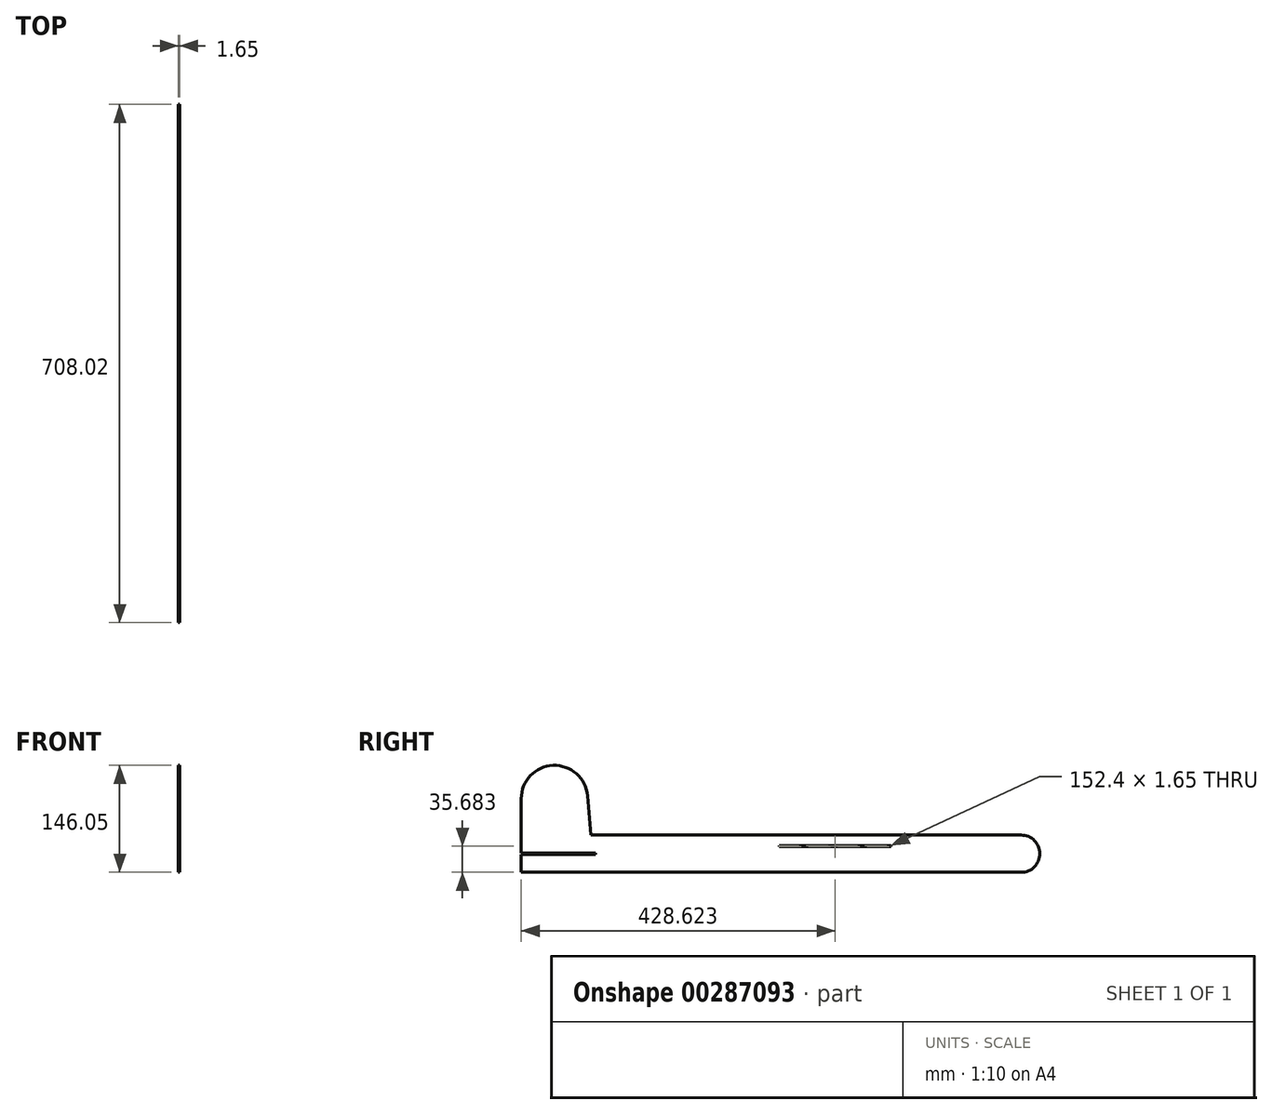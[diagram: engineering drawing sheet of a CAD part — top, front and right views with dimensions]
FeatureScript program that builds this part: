
annotation { "Feature Type Name" : "Feature", "Feature Type Description" : "" }
export const myFeature = defineFeature(function(context is Context, id is Id, definition is map)
    precondition{}
    {
        {
            var Q0;
            Q0=qCreatedBy(makeId("Right.planeOp"),FACE);
            var sketch = newSketch(context, id + "F0", { "sketchPlane" : qUnion([Q0])});
            skLineSegment(sketch, "E0.bottom", {"start": v(-246.06, 25.4) * mm, "end": v(341.31, 25.4) * mm});
            skLineSegment(sketch, "E0.top", {"start": v(-341.31, -25.4) * mm, "end": v(341.31, -25.4) * mm});
            skLineSegment(sketch, "E0.left", {"start": v(-341.31, 25.4) * mm, "end": v(-341.31, -25.4) * mm});
            skPoint(sketch, "E0.middle", {"position": v(0, 0) * mm});
            skLineSegment(sketch, "E1", {"start": v(-246.06, 25.4) * mm, "end": v(-250.77, 79.25) * mm});
            skLineSegment(sketch, "E2", {"start": v(-341.31, 75.3) * mm, "end": v(-341.31, 25.4) * mm});
            skArc(sketch, "E3", {"start": v(-250.77, 79.25) * mm, "mid": v(-297.94, 120.6) * mm, "end": v(-341.31, 75.3) * mm});
            skArc(sketch, "E4", {"start": v(341.31, -25.4) * mm, "mid": v(366.71, 0) * mm, "end": v(341.31, 25.4) * mm});
            skPoint(sketch, "E4.third.point", {"position": v(365.34, 8.24) * mm});
            skSolve(sketch);
        }
        {
            var Q0;
            Q0=makeQuery(id+"F0.imprint","IMPRINT",FACE,{"disambiguationData":[TD([[makeQuery(id+"F0.imprint","IMPRINT",EDGE,{"derivedFrom":sQuery(id+"F0.wireOp",EDGE,"E0.bottom")}),-1.0]])]});
            extrude(context, id + "F1", {"entities" : qUnion([Q0]), "depth" : 1.65 * mm});
        }
        {
            var Q0;
            Q0=makeQuery(id+"F0.imprint","IMPRINT",FACE,{"disambiguationData":[TD([[makeQuery(id+"F0.imprint","IMPRINT",EDGE,{"derivedFrom":sQuery(id+"F0.wireOp",EDGE,"E0.bottom")}),-1.0]])]});
            var sketch = newSketch(context, id + "F2", { "sketchPlane" : qUnion([Q0])});
            skLineSegment(sketch, "E5.bottom", {"start": v(11.11, 11.1) * mm, "end": v(163.51, 11.1) * mm});
            skLineSegment(sketch, "E5.top", {"start": v(11.11, 9.46) * mm, "end": v(163.51, 9.46) * mm});
            skLineSegment(sketch, "E5.left", {"start": v(11.11, 11.1) * mm, "end": v(11.11, 9.46) * mm});
            skLineSegment(sketch, "E5.right", {"start": v(163.51, 11.1) * mm, "end": v(163.51, 9.46) * mm});
            skPoint(sketch, "E5.middle", {"position": v(87.31, 10.28) * mm});
            skLineSegment(sketch, "E6.bottom", {"start": v(-341.31, 0.83) * mm, "end": v(-239.71, 0.83) * mm});
            skLineSegment(sketch, "E6.top", {"start": v(-341.31, -0.83) * mm, "end": v(-239.71, -0.83) * mm});
            skLineSegment(sketch, "E6.left", {"start": v(-341.31, 0.83) * mm, "end": v(-341.31, -0.83) * mm});
            skLineSegment(sketch, "E6.right", {"start": v(-239.71, 0.83) * mm, "end": v(-239.71, -0.83) * mm});
            skPoint(sketch, "E6.middle", {"position": v(-290.51, 0) * mm});
            skSolve(sketch);
        }
        {
            var Q0;
            Q0 = qSketchRegion(id + "F2", true);
            extrude(context, id + "F3", {"entities" : qUnion([Q0]), "operationType" : NewBodyOperationType.REMOVE, "endBound" : BoundingType.SYMMETRIC, "depth" : 25.4 * mm});
        }
    });
